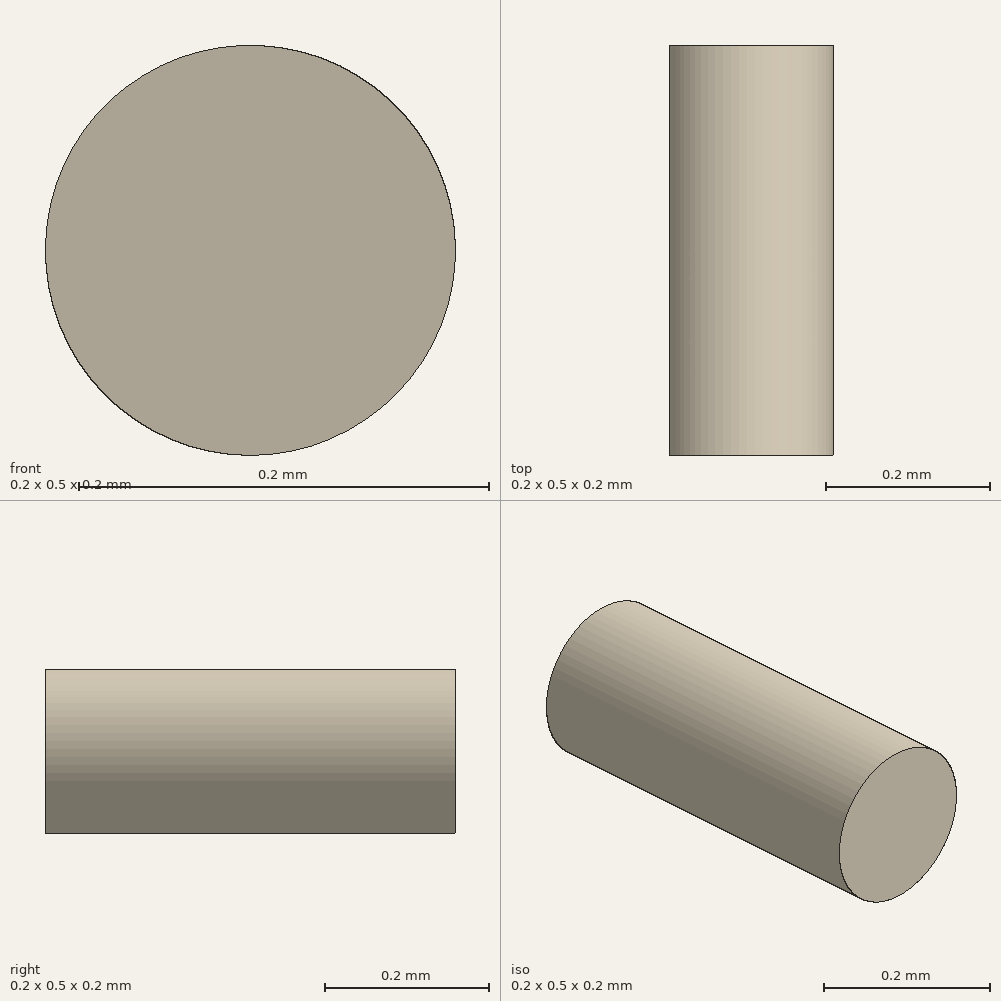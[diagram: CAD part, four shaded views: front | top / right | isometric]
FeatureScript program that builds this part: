
annotation { "Feature Type Name" : "Feature", "Feature Type Description" : "" }
export const myFeature = defineFeature(function(context is Context, id is Id, definition is map)
    precondition{}
    {
        {
            var Q0;
            Q0=qCreatedBy(makeId("Front.planeOp"),FACE);
            var sketch = newSketch(context, id + "F0", { "sketchPlane" : qUnion([Q0])});
            skCircle(sketch, "E0", {"center": v(0, 0) * mm, "radius": 0.1 * mm});
            skSolve(sketch);
        }
        {
            var Q0;
            Q0 = qSketchRegion(id + "F0", true);
            extrude(context, id + "F1", {"entities" : qUnion([Q0]), "depth" : 0.5 * mm, "offsetDistance" : 25 * mm});
        }
    });
